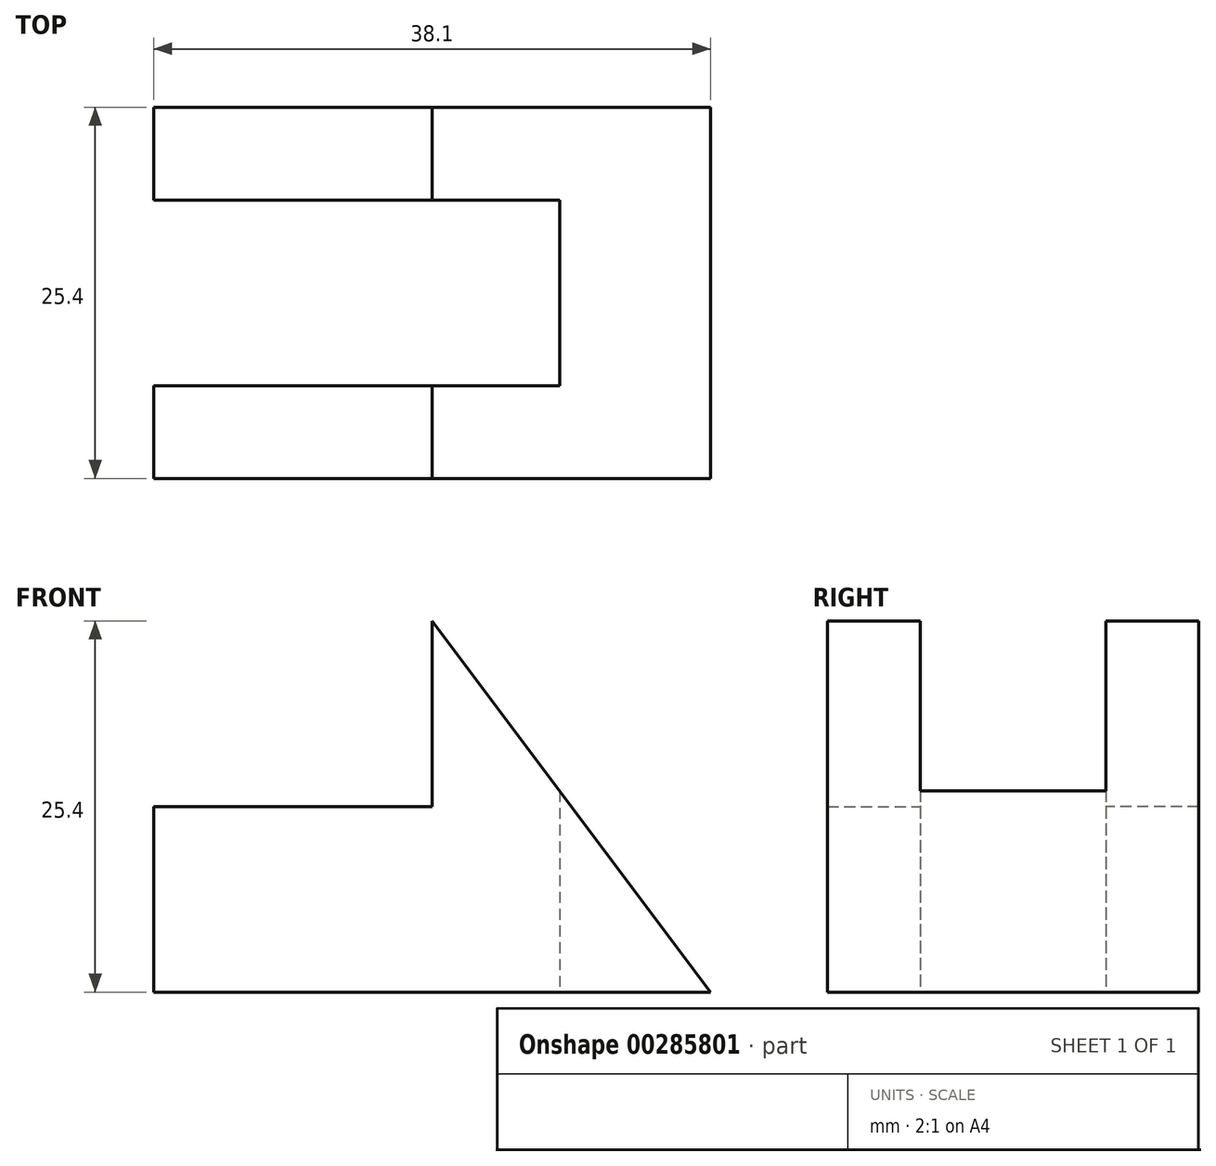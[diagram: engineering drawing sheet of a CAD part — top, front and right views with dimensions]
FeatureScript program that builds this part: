
annotation { "Feature Type Name" : "Feature", "Feature Type Description" : "" }
export const myFeature = defineFeature(function(context is Context, id is Id, definition is map)
    precondition{}
    {
        {
            var Q0;
            Q0=qCreatedBy(makeId("Top.planeOp"),FACE);
            var sketch = newSketch(context, id + "F0", { "sketchPlane" : qUnion([Q0])});
            skLineSegment(sketch, "E0.bottom", {"start": v(-19.05, 25.4) * mm, "end": v(19.05, 25.4) * mm});
            skLineSegment(sketch, "E0.top", {"start": v(-19.05, 0) * mm, "end": v(19.05, 0) * mm});
            skLineSegment(sketch, "E0.left", {"start": v(-19.05, 25.4) * mm, "end": v(-19.05, 0) * mm});
            skLineSegment(sketch, "E0.right", {"start": v(19.05, 25.4) * mm, "end": v(19.05, 0) * mm});
            skLineSegment(sketch, "E1", {"start": v(-19.05, 0) * mm, "end": v(-19.05, 6.35) * mm});
            skLineSegment(sketch, "E2", {"start": v(-19.05, 6.35) * mm, "end": v(8.73, 6.35) * mm});
            skLineSegment(sketch, "E3", {"start": v(8.73, 6.35) * mm, "end": v(8.73, 19.05) * mm});
            skLineSegment(sketch, "E4", {"start": v(8.73, 19.05) * mm, "end": v(-19.05, 19.05) * mm});
            skLineSegment(sketch, "E5", {"start": v(-19.05, 19.05) * mm, "end": v(-19.05, 25.4) * mm});
            skLineSegment(sketch, "E6", {"start": v(0, 25.4) * mm, "end": v(0, 19.05) * mm});
            skLineSegment(sketch, "E7", {"start": v(0, 0) * mm, "end": v(0, 6.35) * mm});
            skSolve(sketch);
        }
        {
            var Q0;
            {var subQ0=sQuery(id+"F0.wireOp",EDGE,"E0.right");Q0=makeQuery(id+"F0.imprint","IMPRINT",FACE,{"disambiguationData":[TD([[makeQuery(id+"F0.imprint","IMPRINT",EDGE,{"derivedFrom":subQ0}),-1.0]])]});}
            var Q1;
            {var subQ0=sQuery(id+"F0.wireOp",EDGE,"E1");Q1=makeQuery(id+"F0.imprint","IMPRINT",FACE,{"disambiguationData":[TD([[makeQuery(id+"F0.imprint","IMPRINT",EDGE,{"derivedFrom":subQ0}),-1.0]])]});}
            var Q2;
            {var subQ0=sQuery(id+"F0.wireOp",EDGE,"E5");Q2=makeQuery(id+"F0.imprint","IMPRINT",FACE,{"disambiguationData":[TD([[makeQuery(id+"F0.imprint","IMPRINT",EDGE,{"derivedFrom":subQ0}),-1.0]])]});}
            extrude(context, id + "F1", {"entities" : qUnion([Q0, Q1, Q2]), "depth" : 25.4 * mm});
        }
        {
            var Q0;
            {var subQ3=sQuery(id+"F0.wireOp",EDGE,"E0.left");Q0=makeQuery(id+"F0.imprint","IMPRINT",FACE,{"disambiguationData":[TD([[makeQuery(id+"F0.imprint","IMPRINT",EDGE,{"derivedFrom":subQ3}),1.0]])]});}
            extrude(context, id + "F2", {"entities" : qUnion([Q0]), "operationType" : NewBodyOperationType.ADD, "depth" : 12.7 * mm});
        }
        {
            var Q0;
            Q0=makeQuery(id+"F1.opExtrude","SWEPT_FACE",FACE,{"disambiguationData":[OSD([sQuery(id+"F0.wireOp",EDGE,"E0.top")])]});
            var sketch = newSketch(context, id + "F3", { "sketchPlane" : qUnion([Q0])});
            skLineSegment(sketch, "E8", {"start": v(-19.05, 25.4) * mm, "end": v(0, 25.4) * mm});
            skLineSegment(sketch, "E9", {"start": v(0, 25.4) * mm, "end": v(19.05, 0) * mm});
            skLineSegment(sketch, "E10", {"start": v(19.05, 0) * mm, "end": v(19.05, 25.4) * mm});
            skLineSegment(sketch, "E11", {"start": v(19.05, 25.4) * mm, "end": v(0, 25.4) * mm});
            skSolve(sketch);
        }
        {
            var Q0;
            Q0=makeQuery(id+"F3.imprint","IMPRINT",FACE,{"disambiguationData":[TD([[makeQuery(id+"F3.imprint","IMPRINT",EDGE,{"derivedFrom":sQuery(id+"F3.wireOp",EDGE,"E9")}),1.0]])]});
            extrude(context, id + "F4", {"entities" : qUnion([Q0]), "operationType" : NewBodyOperationType.REMOVE, "oppositeDirection" : true, "depth" : 25.4 * mm});
        }
    });
